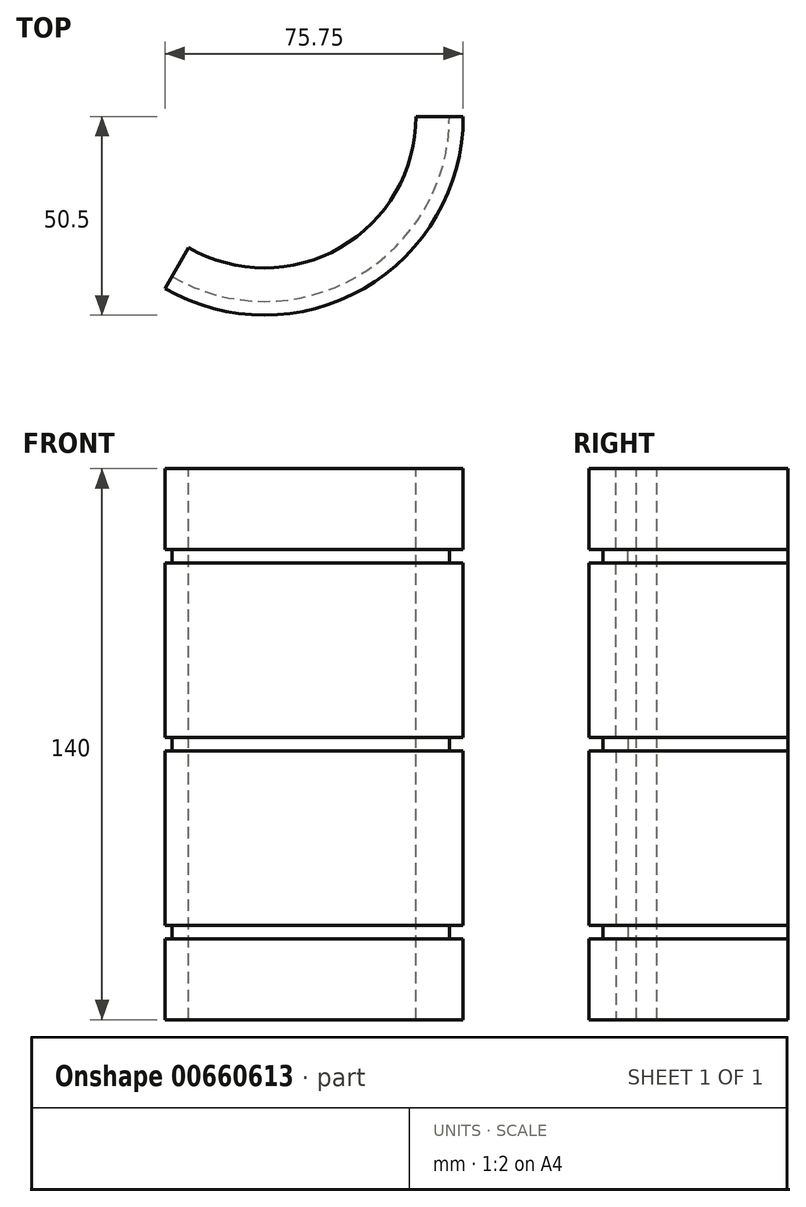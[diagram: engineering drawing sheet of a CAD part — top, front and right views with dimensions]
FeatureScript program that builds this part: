
annotation { "Feature Type Name" : "Feature", "Feature Type Description" : "" }
export const myFeature = defineFeature(function(context is Context, id is Id, definition is map)
    precondition{}
    {
        {
            var Q0;
            Q0=qCreatedBy(makeId("Front.planeOp"),FACE);
            var sketch = newSketch(context, id + "F0", { "sketchPlane" : qUnion([Q0])});
            skLineSegment(sketch, "E0", {"start": v(0, 0) * mm, "end": v(0, 55.16) * mm});
            skLineSegment(sketch, "E1", {"start": v(0, 55.16) * mm, "end": v(0, -58.82) * mm});
            skLineSegment(sketch, "E2", {"start": v(0, 0) * mm, "end": v(38.5, 0) * mm});
            skLineSegment(sketch, "E3", {"start": v(38.5, 0) * mm, "end": v(38.5, 70) * mm});
            skLineSegment(sketch, "E4", {"start": v(47, 0) * mm, "end": v(47, 1.75) * mm});
            skLineSegment(sketch, "E5", {"start": v(47, 1.75) * mm, "end": v(47, 0) * mm});
            skLineSegment(sketch, "E6", {"start": v(47, 1.75) * mm, "end": v(50.5, 1.75) * mm});
            skLineSegment(sketch, "E7", {"start": v(50.5, 1.75) * mm, "end": v(50.5, 46) * mm});
            skLineSegment(sketch, "E8", {"start": v(50.5, 46) * mm, "end": v(47, 46) * mm});
            skLineSegment(sketch, "E9", {"start": v(47, 46) * mm, "end": v(47, 49.5) * mm});
            skLineSegment(sketch, "E10", {"start": v(47, 49.5) * mm, "end": v(50.5, 49.5) * mm});
            skLineSegment(sketch, "E11", {"start": v(38.5, 70) * mm, "end": v(50.5, 70) * mm});
            skLineSegment(sketch, "E12", {"start": v(50.5, 49.5) * mm, "end": v(50.5, 70) * mm});
            skPoint(sketch, "E12.endSnap0", {"position": v(61.95, 70) * mm});
            skPoint(sketch, "E13.orphan", {"position": v(85.4, 70) * mm});
            skPoint(sketch, "E14.MirrorCS.end.orphan", {"position": v(51.25, -70) * mm});
            skPoint(sketch, "E14.MirrorCS.start.orphan", {"position": v(38.5, -70) * mm});
            skLineSegment(sketch, "E15.MirrorCS", {"start": v(47, 0) * mm, "end": v(47, -1.75) * mm});
            skLineSegment(sketch, "E16.MirrorCS", {"start": v(47, -1.75) * mm, "end": v(47, 0) * mm});
            skLineSegment(sketch, "E17.MirrorCS", {"start": v(47, -1.75) * mm, "end": v(50.5, -1.75) * mm});
            skLineSegment(sketch, "E18.MirrorCS", {"start": v(47, -46) * mm, "end": v(47, -49.5) * mm});
            skLineSegment(sketch, "E19.MirrorCS", {"start": v(47, -49.5) * mm, "end": v(50.5, -49.5) * mm});
            skLineSegment(sketch, "E20.MirrorCS", {"start": v(50.5, -46) * mm, "end": v(47, -46) * mm});
            skLineSegment(sketch, "E21.MirrorCS", {"start": v(50.5, -1.75) * mm, "end": v(50.5, -46) * mm});
            skLineSegment(sketch, "E22.MirrorCS", {"start": v(38.5, -70) * mm, "end": v(50.5, -70) * mm});
            skPoint(sketch, "E23.MirrorP", {"position": v(61.95, -70) * mm});
            skLineSegment(sketch, "E24.MirrorCS", {"start": v(50.5, -49.5) * mm, "end": v(50.5, -70) * mm});
            skLineSegment(sketch, "E25.MirrorCS", {"start": v(38.5, 0) * mm, "end": v(38.5, -70) * mm});
            skSolve(sketch);
        }
        {
            var Q0;
            Q0=makeQuery(id+"F0.imprint","IMPRINT",FACE,{"disambiguationData":[TD([[makeQuery(id+"F0.imprint","IMPRINT",EDGE,{"derivedFrom":sQuery(id+"F0.wireOp",EDGE,"E3")}),-1.0]])]});
            var Q1;
            Q1=sQuery(id+"F0.wireOp",EDGE,"E1");
            revolve(context, id + "F1", {"entities" : qUnion([Q0]), "axis" : qUnion([Q1]), "revolveType" : RevolveType.ONE_DIRECTION, "angle" : 120 * degree});
        }
    });
